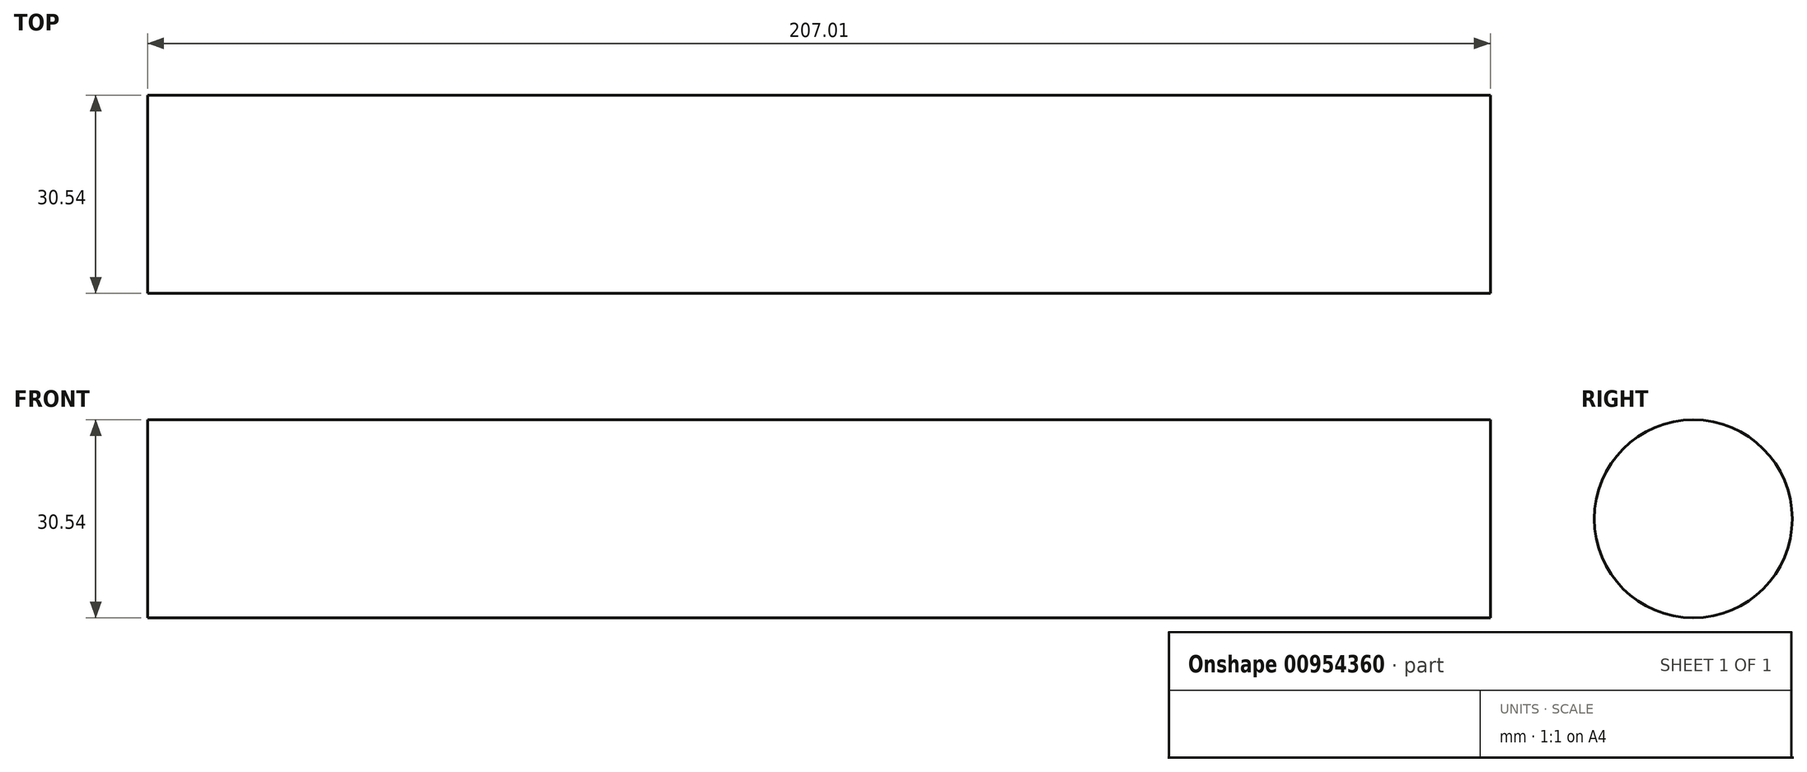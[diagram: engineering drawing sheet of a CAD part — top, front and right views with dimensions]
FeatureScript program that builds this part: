
annotation { "Feature Type Name" : "Feature", "Feature Type Description" : "" }
export const myFeature = defineFeature(function(context is Context, id is Id, definition is map)
    precondition{}
    {
        {
            var Q0;
            Q0=qCreatedBy(makeId("Right.planeOp"),FACE);
            var sketch = newSketch(context, id + "F0", { "sketchPlane" : qUnion([Q0])});
            skCircle(sketch, "E0", {"center": v(0, 0) * mm, "radius": 15.27 * mm});
            skSolve(sketch);
        }
        {
            var Q0;
            Q0 = qSketchRegion(id + "F0", true);
            extrude(context, id + "F1", {"entities" : qUnion([Q0]), "depth" : 207 * mm, "offsetDistance" : 25.4 * mm});
        }
    });
